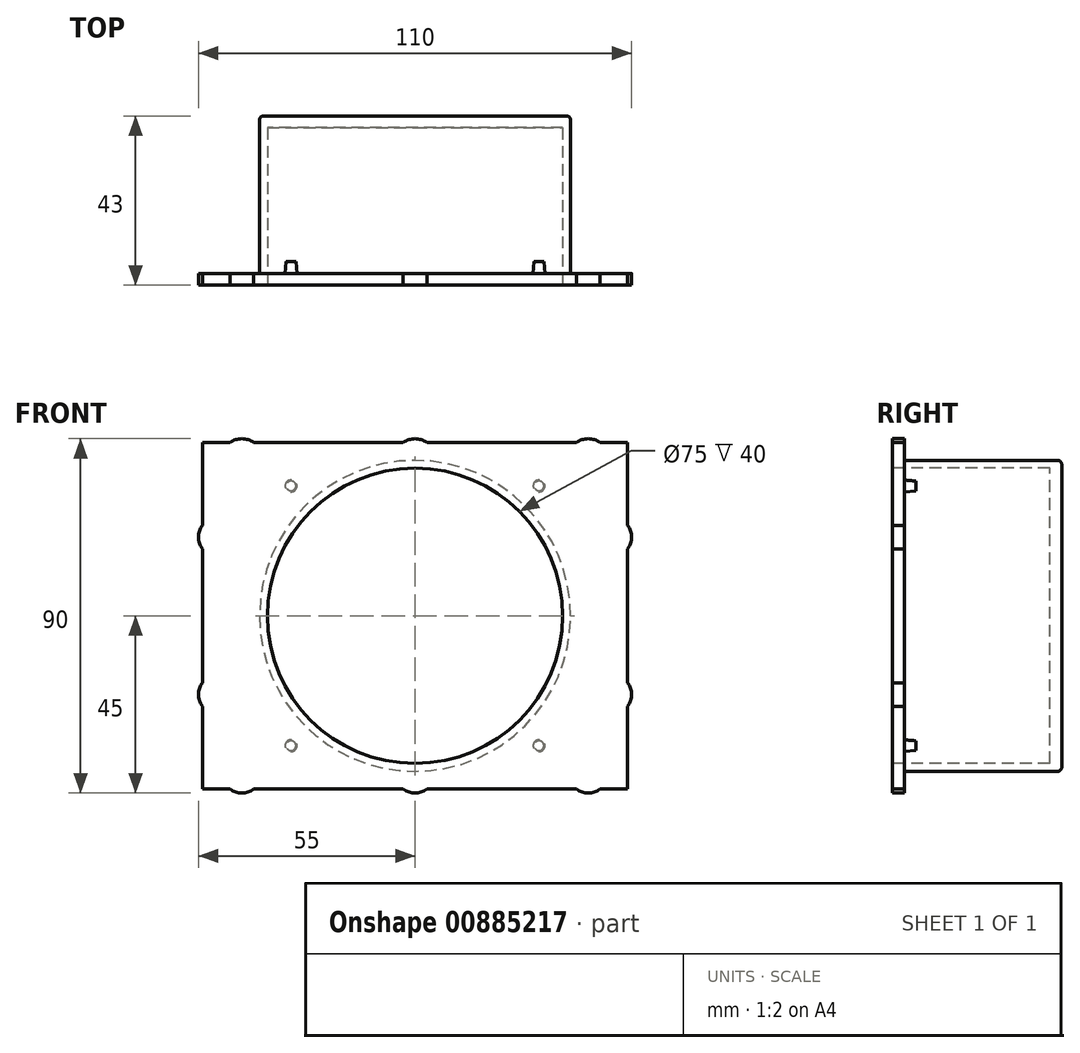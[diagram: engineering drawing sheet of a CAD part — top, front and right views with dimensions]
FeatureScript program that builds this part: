
annotation { "Feature Type Name" : "Feature", "Feature Type Description" : "" }
export const myFeature = defineFeature(function(context is Context, id is Id, definition is map)
    precondition{}
    {
        {
            var Q0;
            Q0=qCreatedBy(makeId("Front.planeOp"),FACE);
            var sketch = newSketch(context, id + "F0", { "sketchPlane" : qUnion([Q0])});
            skLineSegment(sketch, "E0.bottom", {"start": v(0, 0) * mm, "end": v(108, 0) * mm});
            skLineSegment(sketch, "E0.top", {"start": v(0, 88) * mm, "end": v(108, 88) * mm});
            skLineSegment(sketch, "E0.left", {"start": v(0, 0) * mm, "end": v(0, 88) * mm});
            skLineSegment(sketch, "E0.right", {"start": v(108, 0) * mm, "end": v(108, 88) * mm});
            skCircle(sketch, "E1", {"center": v(10, 84) * mm, "radius": 5 * mm});
            skLineSegment(sketch, "E2", {"start": v(54, 88) * mm, "end": v(54, 0) * mm});
            skLineSegment(sketch, "E3", {"start": v(108, 44) * mm, "end": v(0, 44) * mm});
            skCircle(sketch, "E4.MirrorC", {"center": v(98, 84) * mm, "radius": 5 * mm});
            skCircle(sketch, "E5", {"center": v(54, 84) * mm, "radius": 5 * mm});
            skCircle(sketch, "E6.MirrorC", {"center": v(10, 4) * mm, "radius": 5 * mm});
            skCircle(sketch, "E7.MirrorC", {"center": v(54, 4) * mm, "radius": 5 * mm});
            skCircle(sketch, "E8.MirrorC", {"center": v(98, 4) * mm, "radius": 5 * mm});
            skCircle(sketch, "E9.MirrorC", {"center": v(104, 24) * mm, "radius": 5 * mm});
            skCircle(sketch, "E10.MirrorC", {"center": v(4, 24) * mm, "radius": 5 * mm});
            skCircle(sketch, "E11.MirrorC", {"center": v(104, 64) * mm, "radius": 5 * mm});
            skCircle(sketch, "E12.MirrorC", {"center": v(4, 64) * mm, "radius": 5 * mm});
            skSolve(sketch);
        }
        {
            var Q0;
            Q0 = qSketchRegion(id + "F0", true);
            var Q1;
            Q1=makeQuery(id+"F0.imprint","IMPRINT",FACE,{"disambiguationData":[TD([[makeQuery(id+"F0.imprint","IMPRINT",EDGE,{"derivedFrom":sQuery(id+"F0.wireOp",EDGE,"E0.bottom")}),1.0]])]});
            extrude(context, id + "F1", {"entities" : qUnion([Q0, Q1]), "depth" : 3 * mm, "offsetDistance" : 25 * mm});
        }
        {
            var Q0;
            Q0=makeQuery(id+"F1.opExtrude","CAP_FACE",FACE,{"disambiguationData":[OSD([sQuery(id+"F0.wireOp",EDGE,"E0.bottom"),sQuery(id+"F0.wireOp",EDGE,"E0.top"),sQuery(id+"F0.wireOp",EDGE,"E0.left"),sQuery(id+"F0.wireOp",EDGE,"E0.right")])],"isStart":true});
            var sketch = newSketch(context, id + "F2", { "sketchPlane" : qUnion([Q0])});
            skCircle(sketch, "E13", {"center": v(-54, 44) * mm, "radius": 39.5 * mm});
            skSolve(sketch);
        }
        {
            var Q0;
            Q0=makeQuery(id+"F2.imprint","IMPRINT",FACE,{"disambiguationData":[TD([[makeQuery(id+"F2.imprint","IMPRINT",EDGE,{"derivedFrom":sQuery(id+"F2.wireOp",EDGE,"E13")}),1.0]])]});
            extrude(context, id + "F3", {"entities" : qUnion([Q0]), "operationType" : NewBodyOperationType.ADD, "depth" : 40 * mm, "offsetDistance" : 25 * mm});
        }
        {
            var Q0;
            Q0=makeQuery(id+"F1.opExtrude","CAP_FACE",FACE,{"disambiguationData":[OSD([sQuery(id+"F0.wireOp",EDGE,"E0.bottom"),sQuery(id+"F0.wireOp",EDGE,"E0.top"),sQuery(id+"F0.wireOp",EDGE,"E0.left"),sQuery(id+"F0.wireOp",EDGE,"E0.right")])],"isStart":true});
            var sketch = newSketch(context, id + "F4", { "sketchPlane" : qUnion([Q0])});
            skCircle(sketch, "E14", {"center": v(-85.5, 77) * mm, "radius": 1.5 * mm});
            skLineSegment(sketch, "E15", {"start": v(-54, 89) * mm, "end": v(-54, -1) * mm});
            skLineSegment(sketch, "E16", {"start": v(-108, 44) * mm, "end": v(0, 44) * mm});
            skCircle(sketch, "E17.MirrorC", {"center": v(-22.5, 77) * mm, "radius": 1.5 * mm});
            skLineSegment(sketch, "E18.MirrorCS", {"start": v(0, 44) * mm, "end": v(-108, 44) * mm});
            skCircle(sketch, "E19.MirrorC", {"center": v(-85.5, 11) * mm, "radius": 1.5 * mm});
            skCircle(sketch, "E20.MirrorC", {"center": v(-22.5, 11) * mm, "radius": 1.5 * mm});
            skSolve(sketch);
        }
        {
            var Q0;
            Q0 = qSketchRegion(id + "F4", true);
            extrude(context, id + "F5", {"entities" : qUnion([Q0]), "operationType" : NewBodyOperationType.ADD, "depth" : 3 * mm, "offsetDistance" : 25 * mm, "hasDraft" : true, "draftAngle" : 5 * degree, "draftPullDirection" : true});
        }
        {
            var Q0;
            Q0=makeQuery(id+"F3.opExtrude","CAP_EDGE",EDGE,{"disambiguationData":[OSD([sQuery(id+"F2.wireOp",EDGE,"E13")])],"isStart":false});
            fillet(context, id + "F6", {"entities" : qUnion([Q0]), "radius" : 1 * mm, "tangentPropagation" : true, "allowEdgeOverflow" : false});
        }
        {
            var Q0;
            Q0=makeQuery(id+"F1.opExtrude","CAP_FACE",FACE,{"disambiguationData":[OSD([sQuery(id+"F0.wireOp",EDGE,"E0.bottom"),sQuery(id+"F0.wireOp",EDGE,"E0.top"),sQuery(id+"F0.wireOp",EDGE,"E0.left"),sQuery(id+"F0.wireOp",EDGE,"E0.right")])],"isStart":false});
            var sketch = newSketch(context, id + "F7", { "sketchPlane" : qUnion([Q0])});
            skCircle(sketch, "E21", {"center": v(54, 44) * mm, "radius": 37.5 * mm});
            skSolve(sketch);
        }
        {
            var Q0;
            Q0=makeQuery(id+"F7.imprint","IMPRINT",FACE,{"disambiguationData":[TD([[makeQuery(id+"F7.imprint","IMPRINT",EDGE,{"derivedFrom":sQuery(id+"F7.wireOp",EDGE,"E21")}),1.0]])]});
            extrude(context, id + "F8", {"entities" : qUnion([Q0]), "operationType" : NewBodyOperationType.REMOVE, "oppositeDirection" : true, "depth" : 40 * mm, "offsetDistance" : 25 * mm});
        }
    });
